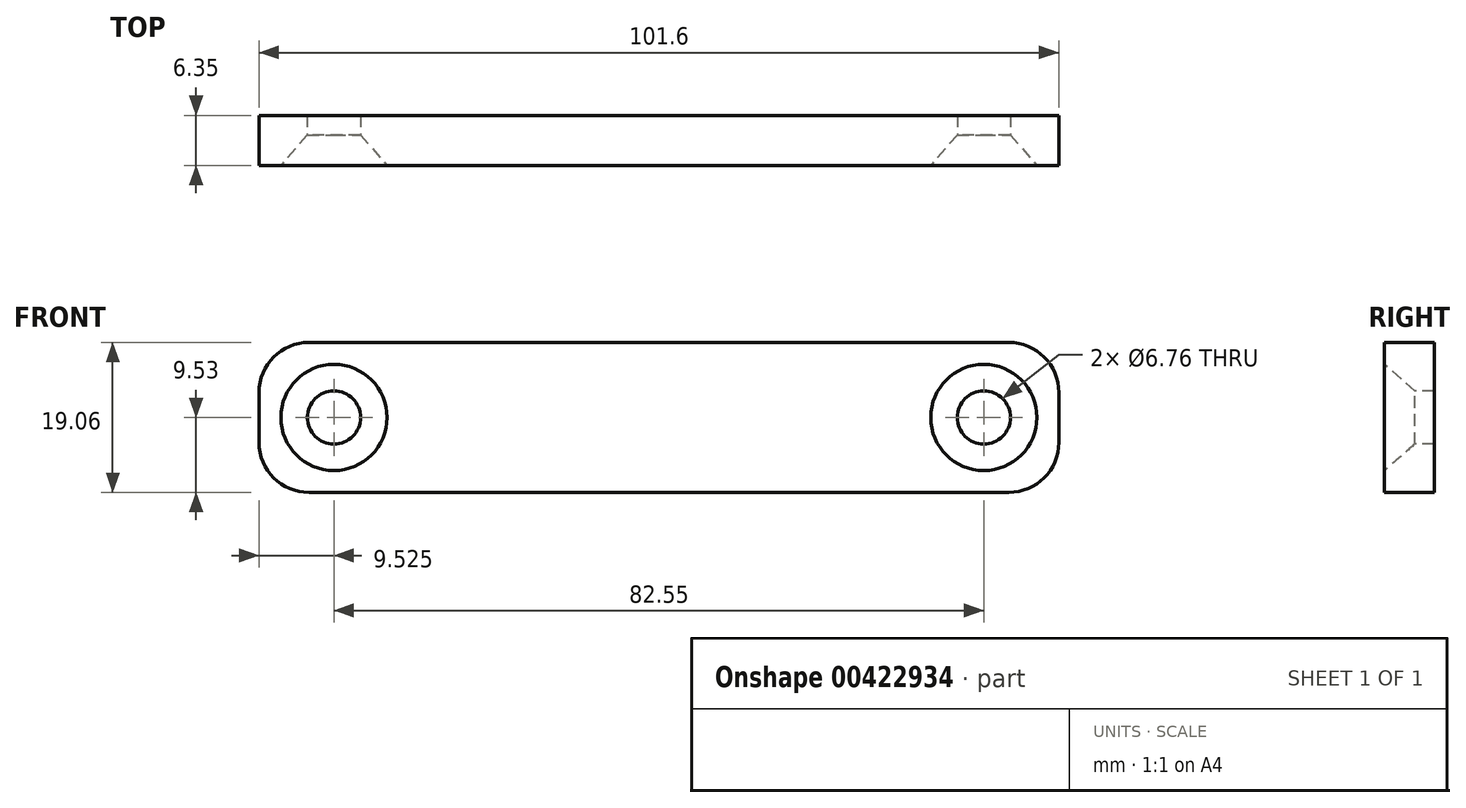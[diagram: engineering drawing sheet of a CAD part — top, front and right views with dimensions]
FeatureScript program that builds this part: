
annotation { "Feature Type Name" : "Feature", "Feature Type Description" : "" }
export const myFeature = defineFeature(function(context is Context, id is Id, definition is map)
    precondition{}
    {
        {
            var Q0;
            Q0=qCreatedBy(makeId("Front.planeOp"),FACE);
            var sketch = newSketch(context, id + "F0", { "sketchPlane" : qUnion([Q0])});
            skLineSegment(sketch, "E0.bottom", {"start": v(50.8, 9.52) * mm, "end": v(-50.8, 9.52) * mm});
            skLineSegment(sketch, "E0.top", {"start": v(50.8, -9.53) * mm, "end": v(-50.8, -9.53) * mm});
            skLineSegment(sketch, "E0.left", {"start": v(50.8, 9.52) * mm, "end": v(50.8, -9.53) * mm});
            skLineSegment(sketch, "E0.right", {"start": v(-50.8, 9.52) * mm, "end": v(-50.8, -9.53) * mm});
            skPoint(sketch, "E0.middle", {"position": v(0, 0) * mm});
            skSolve(sketch);
        }
        {
            var Q0;
            Q0 = qSketchRegion(id + "F0", true);
            extrude(context, id + "F1", {"entities" : qUnion([Q0]), "depth" : 6.35 * mm});
        }
        {
            var Q0;
            Q0=makeQuery(id+"F1.opExtrude","CAP_FACE",FACE,{"disambiguationData":[OSD([sQuery(id+"F0.wireOp",EDGE,"E0.bottom"),sQuery(id+"F0.wireOp",EDGE,"E0.top"),sQuery(id+"F0.wireOp",EDGE,"E0.left"),sQuery(id+"F0.wireOp",EDGE,"E0.right")])],"isStart":false});
            var sketch = newSketch(context, id + "F2", { "sketchPlane" : qUnion([Q0])});
            skCircle(sketch, "E1", {"center": v(41.28, 0) * mm, "radius": 3.18 * mm});
            skCircle(sketch, "E2", {"center": v(-41.28, 0) * mm, "radius": 3.18 * mm});
            skSolve(sketch);
        }
        {
            var Q0;
            Q0=sQuery(id+"F2.wireOp",VERTEX,"E2.center");
            var Q1;
            Q1=sQuery(id+"F2.wireOp",VERTEX,"E1.center");
            var Q2;
            Q2=makeQuery(id+"F1.opExtrude","SWEPT_BODY",BODY,{"disambiguationData":[OSD([sQuery(id+"F0.wireOp",EDGE,"E0.bottom"),sQuery(id+"F0.wireOp",EDGE,"E0.top"),sQuery(id+"F0.wireOp",EDGE,"E0.left"),sQuery(id+"F0.wireOp",EDGE,"E0.right")])]});
            hole(context, id + "F3", {"style" : HoleStyle.C_SINK, "endStyle" : HoleEndStyle.THROUGH, "standardTappedOrClearance" : lookupTablePath({ "standard" : "ANSI", "fit" : "Normal (ASME)", "size" : "1/4", "type" : "Clearance" }), "standardBlindInLast" : lookupTablePath({ "fit" : "Free", "standard" : "ANSI", "size" : "1/4", "type" : "Clearance" }), "holeDiameter" : 6.76 * mm, "cSinkDiameter" : 13.5 * mm, "cSinkAngle" : 82 * degree, "isTappedThrough" : true, "tappedDepth" : 12.7 * mm, "tapClearance" : 3, "locations" : qUnion([Q0, Q1]), "scope" : qUnion([Q2])});
        }
        {
            var Q0;
            Q0=makeQuery(id+"F1.opExtrude","SWEPT_EDGE",EDGE,{"disambiguationData":[OSD([sQuery(id+"F0.wireOp",EDGE,"E0.bottom"),sQuery(id+"F0.wireOp",EDGE,"E0.right")])]});
            var Q1;
            Q1=makeQuery(id+"F1.opExtrude","SWEPT_EDGE",EDGE,{"disambiguationData":[OSD([sQuery(id+"F0.wireOp",EDGE,"E0.top"),sQuery(id+"F0.wireOp",EDGE,"E0.right")])]});
            var Q2;
            Q2=makeQuery(id+"F1.opExtrude","SWEPT_EDGE",EDGE,{"disambiguationData":[OSD([sQuery(id+"F0.wireOp",EDGE,"E0.top"),sQuery(id+"F0.wireOp",EDGE,"E0.left")])]});
            var Q3;
            Q3=makeQuery(id+"F1.opExtrude","SWEPT_EDGE",EDGE,{"disambiguationData":[OSD([sQuery(id+"F0.wireOp",EDGE,"E0.bottom"),sQuery(id+"F0.wireOp",EDGE,"E0.left")])]});
            fillet(context, id + "F4", {"entities" : qUnion([Q0, Q1, Q2, Q3]), "radius" : 6.35 * mm, "tangentPropagation" : true, "allowEdgeOverflow" : false});
        }
    });
